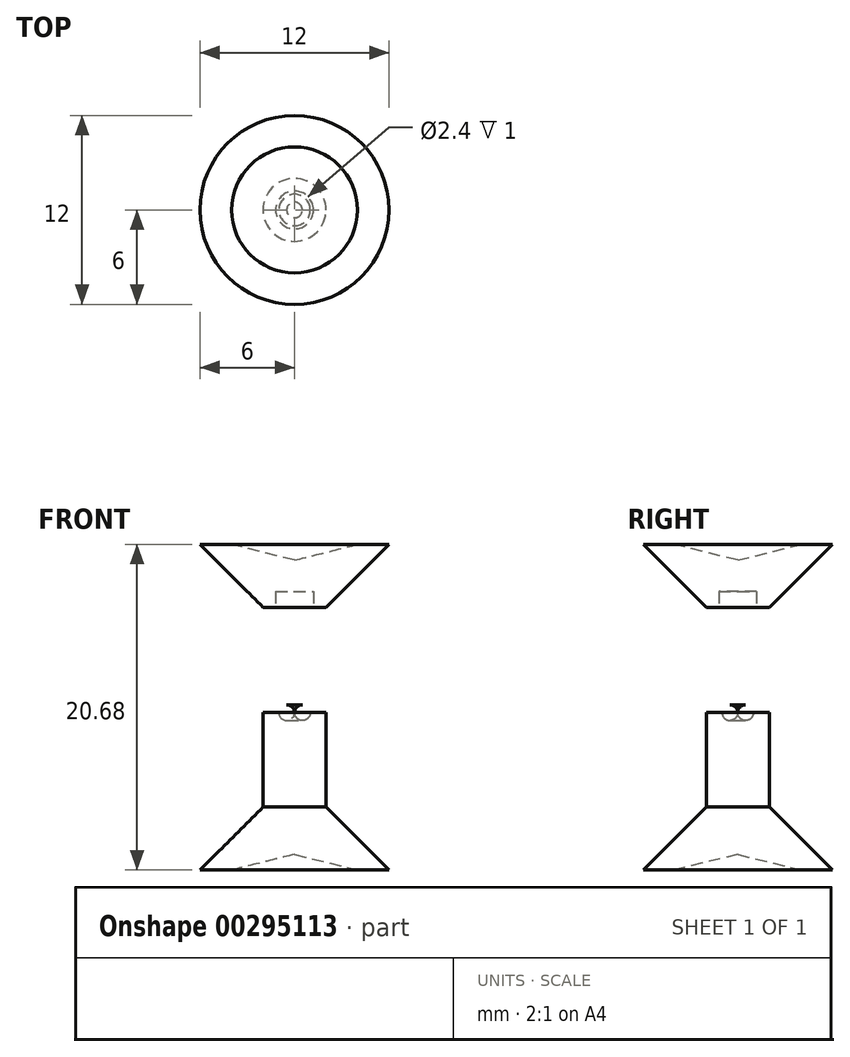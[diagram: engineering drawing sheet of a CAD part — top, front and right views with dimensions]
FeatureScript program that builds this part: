
annotation { "Feature Type Name" : "Feature", "Feature Type Description" : "" }
export const myFeature = defineFeature(function(context is Context, id is Id, definition is map)
    precondition{}
    {
        {
            var Q0;
            Q0=qCreatedBy(makeId("Front.planeOp"),FACE);
            var sketch = newSketch(context, id + "F0", { "sketchPlane" : qUnion([Q0])});
            skLineSegment(sketch, "E0", {"start": v(4, 0) * mm, "end": v(6, 0) * mm});
            skLineSegment(sketch, "E1", {"start": v(6, 0) * mm, "end": v(2, 4) * mm});
            skLineSegment(sketch, "E2", {"start": v(2, 4) * mm, "end": v(2, 10) * mm});
            skLineSegment(sketch, "E3", {"start": v(2, 10) * mm, "end": v(1, 10) * mm});
            skLineSegment(sketch, "E4", {"start": v(1.2, 16.68) * mm, "end": v(2, 16.68) * mm});
            skLineSegment(sketch, "E5", {"start": v(2, 16.68) * mm, "end": v(6, 20.68) * mm});
            skLineSegment(sketch, "E6", {"start": v(6, 20.68) * mm, "end": v(4, 20.68) * mm});
            skLineSegment(sketch, "E7", {"start": v(1.2, 16.68) * mm, "end": v(1.2, 17.68) * mm});
            skLineSegment(sketch, "E8", {"start": v(1.2, 17.68) * mm, "end": v(0, 17.68) * mm});
            skLineSegment(sketch, "E9", {"start": v(1, 10) * mm, "end": v(1, 10) * mm});
            skLineSegment(sketch, "E10", {"start": v(0.5, 10.5) * mm, "end": v(0, 10.5) * mm});
            skPoint(sketch, "E11.orphan", {"position": v(0, 10) * mm});
            skLineSegment(sketch, "E12", {"start": v(0, 1) * mm, "end": v(0, 19.68) * mm, "construction": true});
            skLineSegment(sketch, "E13", {"start": v(0, 17.68) * mm, "end": v(0, 19.68) * mm});
            skLineSegment(sketch, "E14", {"start": v(0, 10.5) * mm, "end": v(0, 1) * mm});
            skPoint(sketch, "E15", {"position": v(0, 19.68) * mm});
            skPoint(sketch, "E16", {"position": v(0, 1) * mm});
            skPoint(sketch, "E17", {"position": v(4, 20.68) * mm});
            skPoint(sketch, "E18", {"position": v(4, 0) * mm});
            skLineSegment(sketch, "E19", {"start": v(4, 20.68) * mm, "end": v(0, 19.68) * mm});
            skLineSegment(sketch, "E20", {"start": v(0, 1) * mm, "end": v(4, 0) * mm});
            skLineSegment(sketch, "E21.trimOffspring", {"start": v(0, 20.68) * mm, "end": v(0, 25.12) * mm, "construction": true});
            skPoint(sketch, "E22.orphan", {"position": v(0, 0) * mm});
            skPoint(sketch, "E23.visualSharp", {"position": v(1, 10.5) * mm});
            skArc(sketch, "E23.filletArc", {"start": v(1, 10) * mm, "mid": v(0.85, 10.35) * mm, "end": v(0.5, 10.5) * mm});
            skSolve(sketch);
        }
        {
            var Q0;
            Q0 = qSketchRegion(id + "F0", true);
            var Q1;
            Q1=sQuery(id+"F0.wireOp",EDGE,"E12");
            revolve(context, id + "F1", {"entities" : qUnion([Q0]), "axis" : qUnion([Q1]), "revolveType" : RevolveType.FULL});
        }
    });
